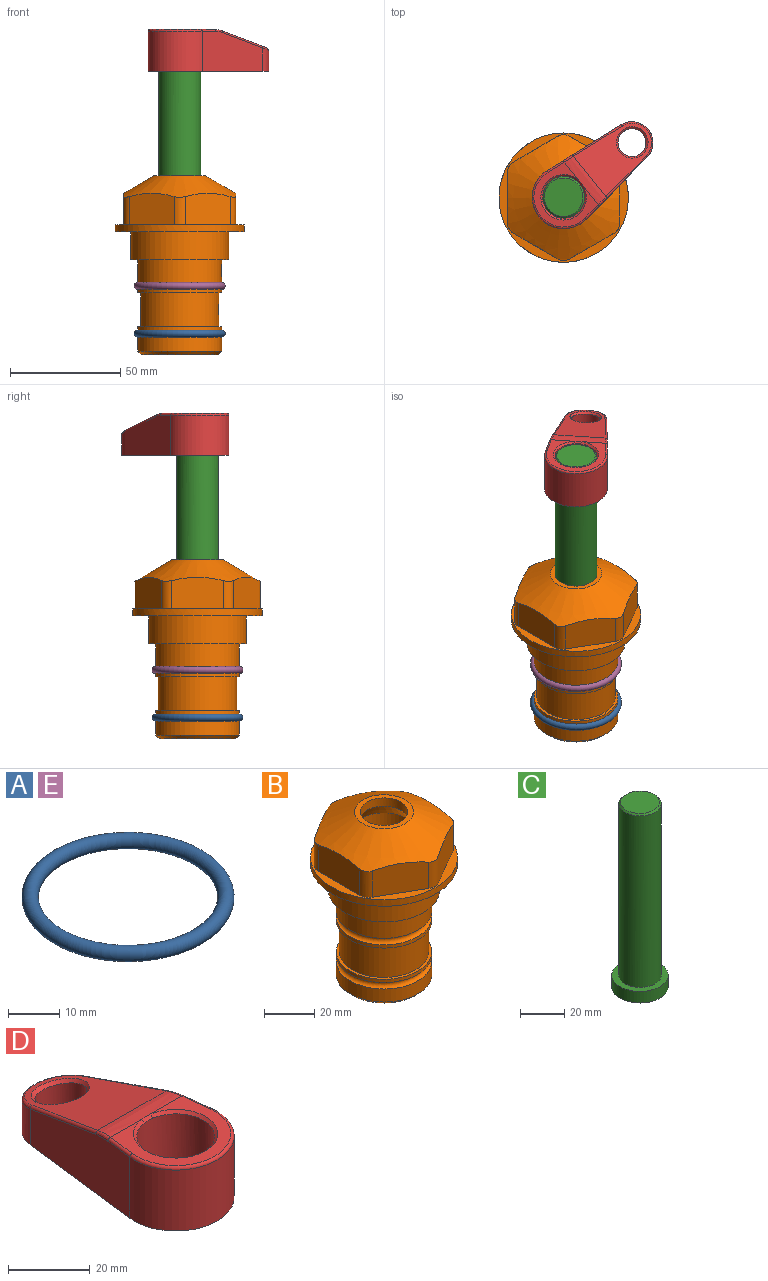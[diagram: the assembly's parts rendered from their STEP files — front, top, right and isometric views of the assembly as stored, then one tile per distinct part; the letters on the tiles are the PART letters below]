
ASSEMBLY  parts=5 mates=4
PART A: 1 faces, bbox 44.7x44.7x3.2 mm
  f0: torus R=19.05mm, axis (0,0,1), area 1193.9mm2
PART B: 36 faces, bbox 58.7x58.7x81 mm
  f0: cylinder r=17.78mm len=35.56mm, axis (0,0,1), area 1670.8mm2, adj f23,f24,f31
  f1: cylinder r=19.05mm len=38.1mm, axis (0,0,1), area 1191.9mm2, adj f26,f27,f30
  f2: plane 58.66x58.66mm, normal (0,0,-1), area 1150.6mm2, adj f3,f28
  f3: cylinder r=29.33mm len=58.66mm, axis (0,0,-1), area 585.1mm2, adj f2,f4
  f4: plane 58.66x58.66mm, normal (0,0,1), area 475.9mm2, adj f3,f5,f6,f7,f8,f9,f10,f11
  f5: plane 20.32x14.34mm, normal (-0.5,0.87,0), area 324.4mm2, adj f4,f15,f16,f17
  f6: plane 20.32x14.34mm, normal (0.5,0.87,0), area 324.4mm2, adj f4,f14,f15,f17
  f7: plane 23.48x14.34mm, normal (1,0,0), area 324.4mm2, adj f4,f13,f14,f17
  f8: plane 20.32x14.34mm, normal (0.5,-0.87,0), area 324.4mm2, adj f4,f12,f13,f17
  f9: plane 20.32x14.34mm, normal (-0.5,-0.87,0), area 324.4mm2, adj f4,f11,f12,f17
  f10: plane 23.48x14.34mm, normal (-1,0,0), area 324.4mm2, adj f4,f11,f16,f17
  f11: cylinder r=5.08mm len=12.85mm, axis (0,0,-1), area 67.2mm2, adj f4,f9,f10,f17
  f12: cylinder r=5.08mm len=12.85mm, axis (0,0,-1), area 67.2mm2, adj f4,f8,f9,f17
  f13: cylinder r=5.08mm len=12.85mm, axis (0,0,-1), area 67.2mm2, adj f4,f7,f8,f17
  f14: cylinder r=5.08mm len=12.85mm, axis (0,0,-1), area 67.2mm2, adj f4,f6,f7,f17
  f15: cylinder r=5.08mm len=12.85mm, axis (0,0,-1), area 67.2mm2, adj f4,f5,f6,f17
  f16: cylinder r=5.08mm len=12.85mm, axis (0,0,-1), area 67.2mm2, adj f4,f5,f10,f17
  f17: cone r=11.73mm half-angle=60deg, axis (0,0,-1), area 2071.8mm2, adj f5,f6,f7,f8,f9,f10,f11,f12
  f18: plane 23.46x23.46mm, normal (0,0,1), area 147.4mm2, adj f17,f35
  f19: plane 34.93x34.93mm, normal (0,0,-1), area 958mm2, adj f29
  f20: cylinder r=19.05mm len=38.1mm, axis (0,0,1), area 760.1mm2, adj f21,f29
  f21: torus R=19.05mm, axis (0,0,1), area 565.3mm2, adj f20,f22
  f22: cylinder r=19.05mm len=38.1mm, axis (0,0,1), area 190mm2, adj f21,f23
  f23: plane 38.1x38.1mm, normal (0,0,1), area 146.9mm2, adj f0,f22
  f24: plane 38.1x38.1mm, normal (0,0,-1), area 146.9mm2, adj f0,f25
  f25: cylinder r=19.05mm len=38.1mm, axis (0,0,1), area 190mm2, adj f24,f26
  f26: torus R=19.05mm, axis (0,0,1), area 565.3mm2, adj f1,f25
  f27: plane 44.45x44.45mm, normal (0,0,-1), area 411.7mm2, adj f1,f28
  f28: cylinder r=22.23mm len=44.45mm, axis (0,0,1), area 1773.5mm2, adj f2,f27
  f29: cone r=19.05mm half-angle=45deg, axis (0,0,1), area 257.5mm2, adj f19,f20
  f30: cylinder r=3.17mm len=6.75mm, axis (-1,0,0), area 128mm2, adj f1,f33
  f31: cylinder r=3.17mm len=6.35mm, axis (-1,0,0), area 102.5mm2, adj f0,f33
  f32: plane 25.4x25.4mm, normal (0,0,1), area 506.7mm2, adj f33
  f33: cylinder r=12.7mm len=66.42mm, axis (0,0,-1), area 5236.2mm2, adj f30,f31,f32,f34
  f34: cone r=9.53mm half-angle=30deg, axis (0,0,-1), area 443.4mm2, adj f33,f35
  f35: cylinder r=9.53mm len=19.05mm, axis (0,0,-1), area 240.9mm2, adj f18,f34
PART C: 6 faces, bbox 25.4x25.4x101.6 mm
  f0: plane 17.46x17.46mm, normal (0,0,1), area 239.5mm2, adj f5
  f1: plane 25.4x25.4mm, normal (0,0,-1), area 506.7mm2, adj f2
  f2: cylinder r=12.7mm len=25.4mm, axis (0,0,1), area 506.7mm2, adj f1,f3
  f3: plane 25.4x25.4mm, normal (0,0,1), area 221.7mm2, adj f2,f4
  f4: cylinder r=9.53mm len=94.46mm, axis (0,0,1), area 5653mm2, adj f3,f5
  f5: cone r=8.73mm half-angle=45deg, axis (0,0,-1), area 64.4mm2, adj f0,f4
PART D: 31 faces, bbox 31.7x65.5x19.8 mm
  f0: plane 39.12x18.26mm, normal (0.99,0.12,0), area 612.2mm2, adj f1,f4,f7,f11,f13,f15
  f1: cylinder r=9.53mm len=18.91mm, axis (0,0,-1), area 296.1mm2, adj f0,f2,f7,f17
  f2: plane 39.12x18.26mm, normal (-0.99,0.12,0), area 612.2mm2, adj f1,f4,f7,f12,f14,f16
  f3: cylinder r=6.35mm len=12.7mm, axis (0,0,-1), area 362.4mm2, adj f7,f18
  f4: cylinder r=14.29mm len=28.58mm, axis (0,0,-1), area 882.2mm2, adj f0,f2,f7,f10
  f5: cylinder r=9.53mm len=19.05mm, axis (0,0,-1), area 1092.6mm2, adj f7,f19,f20
  f6: plane 26.99x23.69mm, normal (0,0,1), area 216.2mm2, adj f9,f10,f11,f12,f19
  f7: plane 63.5x28.58mm, normal (0,0,-1), area 661.8mm2, adj f0,f1,f2,f3,f4,f5,f22,f23
  f8: plane 33.52x23.6mm, normal (0,0.26,0.97), area 486mm2, adj f9,f15,f16,f17,f18
  f9: cylinder r=19.05mm len=24.72mm, axis (1,0,0), area 120.4mm2, adj f6,f8,f13,f14,f20
  f10: torus R=13.49mm, axis (0,0,1), area 59mm2, adj f4,f6,f11,f12
  f11: cylinder r=0.79mm len=8.67mm, axis (0.12,-0.99,0), area 10.8mm2, adj f0,f6,f10,f13
  f12: cylinder r=0.79mm len=8.67mm, axis (0.12,0.99,0), area 10.8mm2, adj f2,f6,f10,f14
  f13: bspline ~4.95x1.42mm, area 6.1mm2, adj f0,f9,f11,f15
  f14: bspline ~4.95x1.42mm, area 6.1mm2, adj f2,f9,f12,f16
  f15: cylinder r=0.79mm len=25.95mm, axis (0.12,-0.96,0.26), area 32.9mm2, adj f0,f8,f13,f17
  f16: cylinder r=0.79mm len=25.95mm, axis (0.12,0.96,-0.26), area 32.9mm2, adj f2,f8,f14,f17
  f17: bspline ~18.91x8.38mm, area 30mm2, adj f1,f8,f15,f16
  f18: bspline ~14.29x14.29mm, area 48.3mm2, adj f3,f8
  f19: cone r=9.53mm half-angle=45deg, axis (0,0,1), area 66.5mm2, adj f5,f6,f20
  f20: bspline ~3.22x0.96mm, area 3.5mm2, adj f5,f9,f19
  f21: plane 2.75x2.72mm, normal (0,0,-1), area 2.9mm2, adj f23,f25,f28
  f22: plane 23.05x15.88mm, normal (-0.99,-0.12,0), area 323.6mm2, adj f7,f25,f26,f27,f28,f29
  f23: plane 23.05x15.88mm, normal (0.99,-0.12,0), area 323.6mm2, adj f7,f21,f25,f27,f28,f30
  f24: cylinder r=9.53mm len=10.69mm, axis (0,0,-1), area 114.7mm2, adj f7,f27,f29,f30
  f25: cylinder r=12.7mm len=20.59mm, axis (0,0,-1), area 381.1mm2, adj f7,f21,f22,f23,f26,f28
  f26: plane 2.75x2.72mm, normal (0,0,-1), area 2.9mm2, adj f22,f25,f28
  f27: plane 19.72x18.37mm, normal (0,-0.26,-0.97), area 291.8mm2, adj f22,f23,f24,f28,f29,f30
  f28: cylinder r=15.88mm len=19.92mm, axis (1,0,0), area 54.8mm2, adj f21,f22,f23,f25,f26,f27
  f29: cylinder r=1.59mm len=11mm, axis (0,0,-1), area 34.7mm2, adj f7,f22,f24,f27
  f30: cylinder r=1.59mm len=11mm, axis (0,0,-1), area 34.7mm2, adj f7,f23,f24,f27
PART E: same geometry as A
PLACE A t=(0,0,-21.59)mm
PLACE B at identity fixed
PLACE C rot(axis=(0,0,-1),51.3deg) t=(0,0,27.55)mm
PLACE D rot(axis=(0,0,-1),51.3deg) t=(0,0,28.35)mm
PLACE E at identity
MATE cylindrical B.f0 <-> C.f2  axis (0,0,1) through (0,0,-50.55)mm
MATE fastened D.f4 <-> C.f2  axis (0,0,-1) through (0,0,91.05)mm
MATE fastened A.f0 <-> B.f0  axis (0,0,1) through (0,0,-46.1)mm
MATE fastened E.f0 <-> B.f0  axis (0,0,1) through (0,0,-24.51)mm
